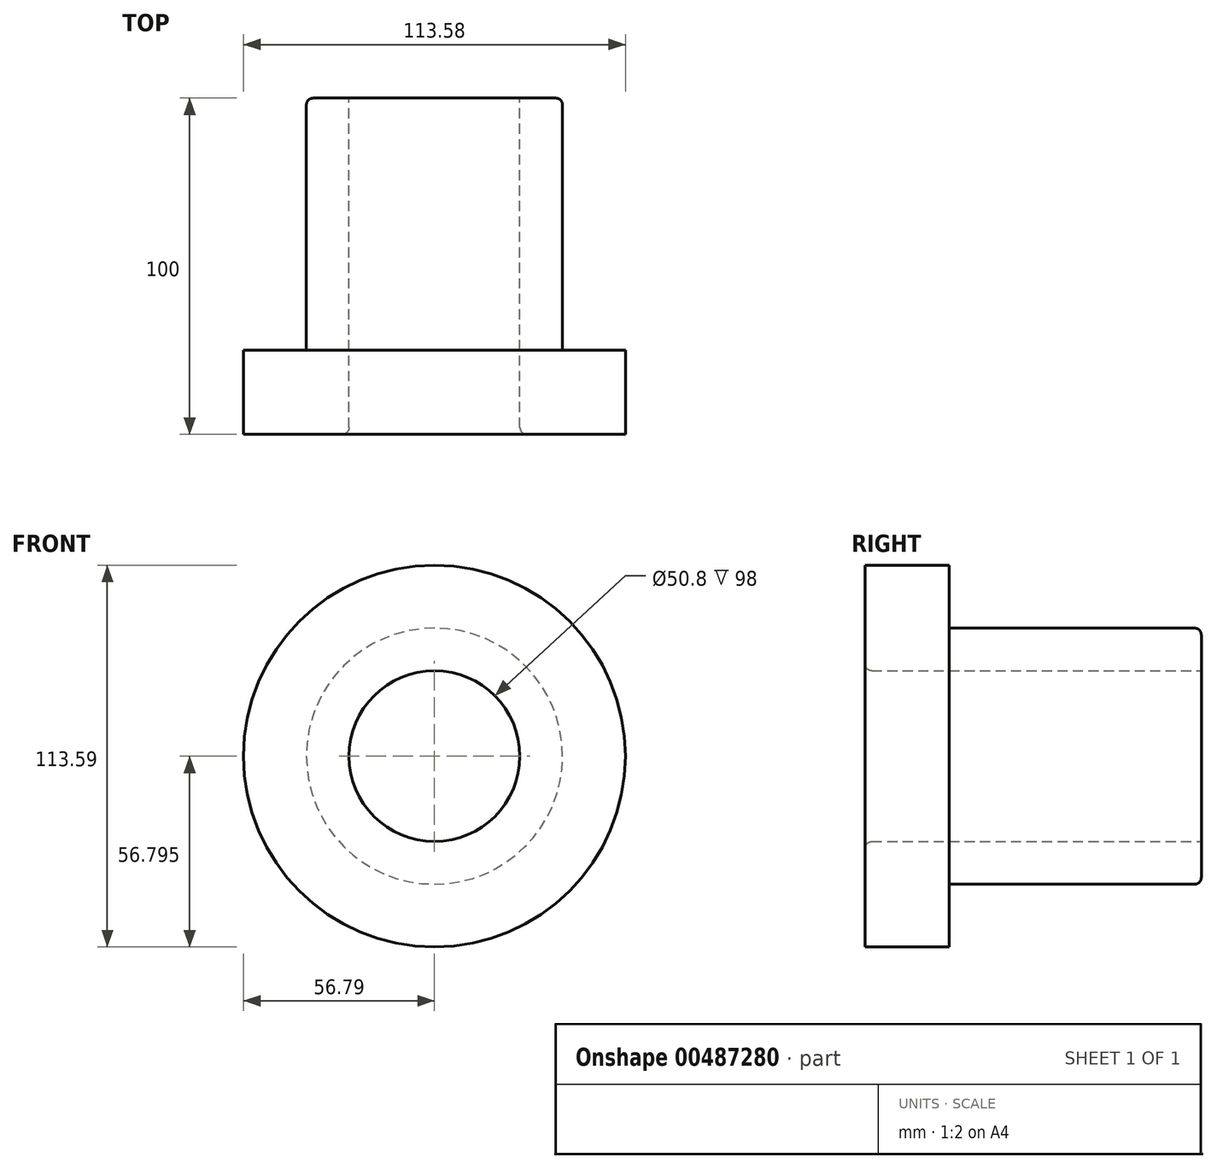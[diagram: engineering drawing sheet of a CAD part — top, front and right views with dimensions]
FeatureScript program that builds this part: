
annotation { "Feature Type Name" : "Feature", "Feature Type Description" : "" }
export const myFeature = defineFeature(function(context is Context, id is Id, definition is map)
    precondition{}
    {
        {
            var Q0;
            Q0=qCreatedBy(makeId("Front.planeOp"),FACE);
            var sketch = newSketch(context, id + "F0", { "sketchPlane" : qUnion([Q0])});
            skCircle(sketch, "E0", {"center": v(0, 36.86) * mm, "radius": 38.1 * mm});
            skCircle(sketch, "E1", {"center": v(0, 36.86) * mm, "radius": 25.4 * mm});
            skSolve(sketch);
        }
        {
            var Q0;
            Q0 = qSketchRegion(id + "F0", true);
            extrude(context, id + "F1", {"entities" : qUnion([Q0]), "depth" : 100 * mm});
        }
        {
            var Q0;
            Q0=makeQuery(id+"F1.opExtrude","CAP_FACE",FACE,{"disambiguationData":[OSD([sQuery(id+"F0.wireOp",EDGE,"E0"),sQuery(id+"F0.wireOp",EDGE,"E1")])],"isStart":false});
            var sketch = newSketch(context, id + "F2", { "sketchPlane" : qUnion([Q0])});
            skCircle(sketch, "E2", {"center": v(0, 36.86) * mm, "radius": 25.41 * mm});
            skCircle(sketch, "E3", {"center": v(0, 36.86) * mm, "radius": 56.8 * mm});
            skSolve(sketch);
        }
        {
            var Q0;
            Q0 = qSketchRegion(id + "F2", true);
            extrude(context, id + "F3", {"entities" : qUnion([Q0]), "operationType" : NewBodyOperationType.ADD, "oppositeDirection" : true, "depth" : 25 * mm});
        }
        {
            var Q0;
            Q0=makeQuery(id+"F1.opExtrude","CAP_EDGE",EDGE,{"disambiguationData":[OSD([sQuery(id+"F0.wireOp",EDGE,"E0")])],"isStart":true});
            fillet(context, id + "F4", {"entities" : qUnion([Q0]), "radius" : 2 * mm, "tangentPropagation" : true, "allowEdgeOverflow" : false});
        }
        {
            var Q0;
            Q0=makeQuery(id+"F1.opExtrude","CAP_EDGE",EDGE,{"disambiguationData":[OSD([sQuery(id+"F0.wireOp",EDGE,"E1")])],"isStart":false});
            fillet(context, id + "F5", {"entities" : qUnion([Q0]), "radius" : 2 * mm, "tangentPropagation" : true, "allowEdgeOverflow" : false});
        }
    });
